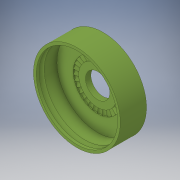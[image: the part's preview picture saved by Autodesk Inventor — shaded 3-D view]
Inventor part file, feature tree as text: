
AUTODESK INVENTOR PART (.ipt)
format: ipt  version: 2018 (Build 220112000, 112)  size: 345,600 bytes
history: native  units: in
note: dims shown in document units (in); Inventor stores cm internally (conversion verified against a paired STEP export)
features: sketch x5, extrude x4, projected_geometry x2, pattern_circular x1, revolve x1
ambient origin geometry x8: Origin, YZ Plane, XZ Plane, XY Plane, X Axis, Y Axis, Z Axis, Center Point
bodies: Solid1 (feature_tree)
feature tree (13):
  extrude  "Extrusion1"  Depth=0.125in TaperAngle=0.0deg
  extrude  "Extrusion2"  Depth=1.75in
  extrude  "Extrusion3"  Depth=0.125in TaperAngle=0.0deg
  pattern_circular  "Circular Pattern1"  [2 undecoded]
  extrude  "Extrusion4"  Depth=1.875in TaperAngle=360.0deg
  revolve  "Revolution1"  [1 undecoded]
  sketch  "Sketch1"  dims[d0=3.998in d1=0.125in d2=0.0in]
  sketch  "Sketch3"  dims[d3=0.375in d4=1.75in]
  sketch  "Sketch4"  dims[d6=0.25in d7=0.125in d8=0.0in]
  sketch  "Sketch5"  dims[d9=0.125in]
  projected_geometry  "Projected Loop1"
  sketch  "Sketch6"  dims[d10=0.0625in d11=1.25in d12=0.0in d13=11.811in d14=360.0deg d16=0.125in d17=1.75in d18=2.25in d19=0.125in d20=1.25in d21=0.0in d22=1.125in d23=0.135in d24=0.706in d26=1.875in d27=0.956in d29=0.0675in d30=0.0675in d31=1.875in d32=90.0deg]
  projected_geometry  "Projected Loop2"
note: 3 required parameter values undecoded (feature->parameter linkage not recoverable at this tier; creation-order binding heuristic only, values carry confidence <= 0.55)